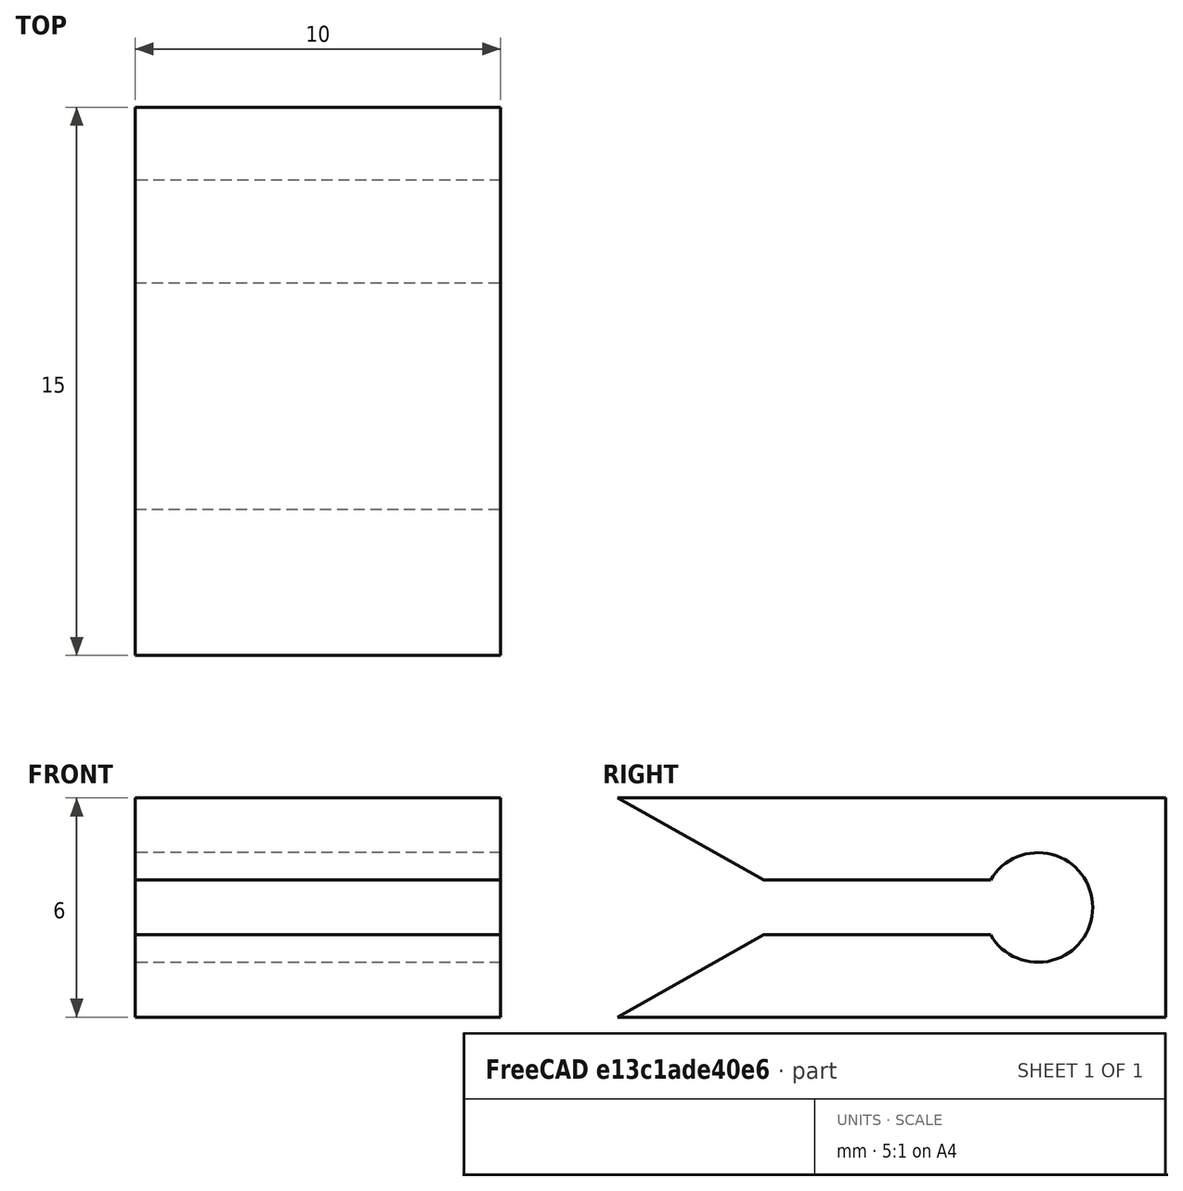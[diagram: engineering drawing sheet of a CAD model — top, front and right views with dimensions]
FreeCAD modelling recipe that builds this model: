
FCSTD DOCUMENT  (FreeCAD 1.0R39285 (Git))
Label: baffle outer clip 2
License: All rights reserved
LicenseURL: https://en.wikipedia.org/wiki/All_rights_reserved
objects: Sketcher::SketchObject×1, PartDesign::Pad×1, PartDesign::Body×1
note: 6 computed .brp shape members not serialized (recipe doc carries the construction recipe); baked Part::Feature solids carry a one-line shape summary decoded from their .brp

FEATURE [Sketcher::SketchObject] Sketch
  ArcFitTolerance = 1e-06
  AttachmentSupport = -> [YZ_Plane]
  FullyConstrained = true
  MakeInternals = false
  MapMode = 5
  Placement = pos=(0,0,0) rot=(0.57735,0.57735,0.57735;2.0944rad)
  sketch-geometry (10):
    g0: ArcOfCircle CenterX=0 CenterY=0 CenterZ=0 NormalX=0 NormalY=0 NormalZ=1 AngleXU=0 Radius=1.5 StartAngle=3.66519 EndAngle=8.90118
    g1: LineSegment StartX=-11.5 StartY=3 StartZ=0 EndX=3.5 EndY=3 EndZ=0
    g2: LineSegment StartX=-11.5 StartY=-3 StartZ=0 EndX=3.5 EndY=-3 EndZ=0
    g3: LineSegment StartX=3.5 StartY=-3 StartZ=0 EndX=3.5 EndY=3 EndZ=0
    g4: LineSegment StartX=-1.29904 StartY=-0.75 StartZ=0 EndX=-7.5 EndY=-0.75 EndZ=0
    g5: LineSegment StartX=-7.5 StartY=-0.75 StartZ=0 EndX=-11.5 EndY=-3 EndZ=0
    g6: LineSegment StartX=-1.29904 StartY=0.75 StartZ=0 EndX=-7.5 EndY=0.75 EndZ=0
    g7: LineSegment StartX=-7.5 StartY=0.75 StartZ=0 EndX=-11.5 EndY=3 EndZ=0
    g8: GeomPoint X=3.5 Y=0 Z=0
    g9: GeomPoint X=1.5 Y=0 Z=0
  constraints (25):
    c: Coincident(g0,g-1)
    c: Diameter(g0) = 3
    c: Vertical(g0,g0)
    c: DistanceY(g0,g0) = 1.5
    c: Horizontal(g1)
    c: Coincident(g3,g2)
    c: Coincident(g3,g1)
    c: DistanceX(g1,g1) = 15
    c: Coincident(g4,g0)
    c: Coincident(g5,g4)
    c: Coincident(g6,g0)
    c: Horizontal(g6)
    c: Coincident(g7,g6)
    c: Symmetric(g6,g4,g-1)
    c: DistanceX(g1,g6) = 4
    c: Symmetric(g1,g2,g-1)
    c: DistanceY(g3,g3) = 6
    c: Coincident(g7,g1)
    c: Coincident(g2,g5)
    c: Symmetric(g2,g1,g-1)
    c: PointOnObject(g8,g3)
    c: PointOnObject(g8,g-1)
    c: PointOnObject(g9,g0)
    c: PointOnObject(g9,g-1)
    c: DistanceX(g9,g8) = 2
FEATURE [PartDesign::Pad] Pad
  Direction = (1,0,0)
  Length = 10
  Length2 = 10
  Midplane = true
  Placement = pos=(0,0,0) rot=(1,1,1;2.0944rad)
  Profile = -> Sketch
  ReferenceAxis = -> Sketch [N_Axis]
  Refine = true
  Suppressed = false
  Type = 0
FEATURE [PartDesign::Body] Body
  AllowCompound = false
  Group = -> [Sketch,Pad]
  Origin = -> Origin
  Tip = -> Pad
